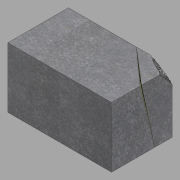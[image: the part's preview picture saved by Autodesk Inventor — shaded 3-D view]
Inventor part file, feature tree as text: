
AUTODESK INVENTOR PART (.ipt)
format: ipt  version: 2022.1 (Build 261234020, 234B)  size: 466,432 bytes
history: native  units: in
note: dims shown in document units (in); Inventor stores cm internally (conversion verified against a paired STEP export)
features: sketch x4, other x3, extrude x1, loft x1
ambient origin geometry x8: Origin, YZ Plane, XZ Plane, XY Plane, X Axis, Y Axis, Z Axis, Center Point
bodies: Solid1 (feature_tree)
feature tree (9):
  other  "2nd.ipt"
  sketch  "Sketch1"  dims[d0=0.3937in d1=1.0in d2=0.0in]
  extrude  "Extrusion1"  Depth=0.3937in TaperAngle=0.0deg
  loft  "Loft1"
  other  "Solid1::2nd.ipt"
  other  "TaggingFeature1"
  sketch  "Sketch2"  dims[d3=0.0in d4=90.0deg d5=0.0in d6=90.0deg]
  sketch  "Sketch3"
  sketch  "Sketch4"
